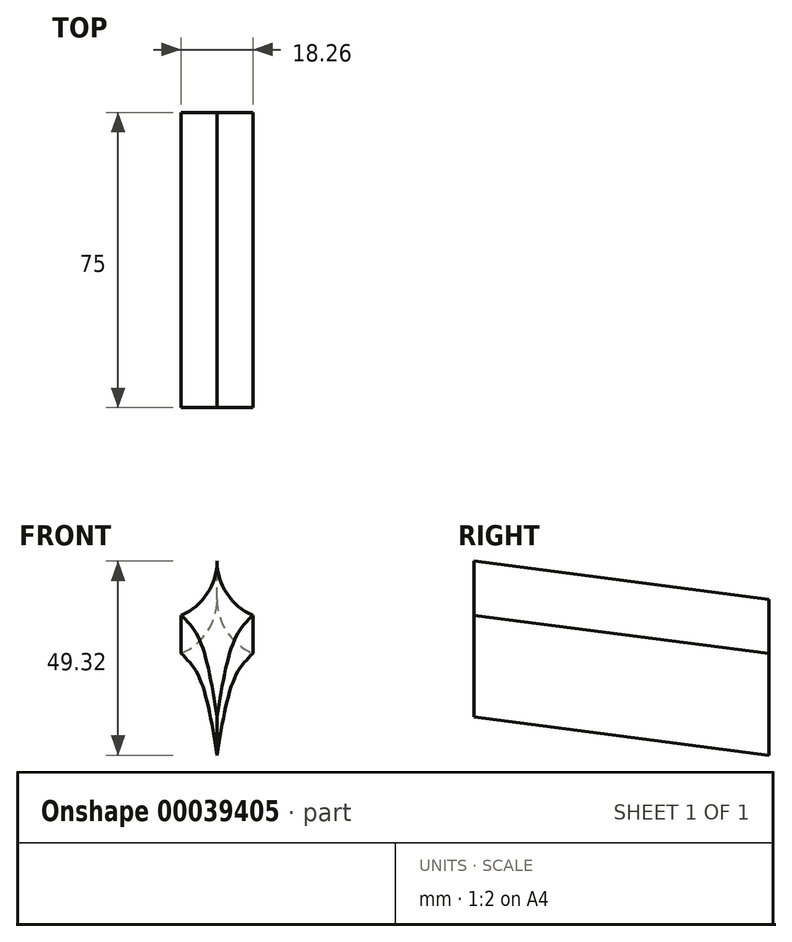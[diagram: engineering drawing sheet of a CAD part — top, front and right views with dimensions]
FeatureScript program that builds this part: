
annotation { "Feature Type Name" : "Feature", "Feature Type Description" : "" }
export const myFeature = defineFeature(function(context is Context, id is Id, definition is map)
    precondition{}
    {
        {
            var Q0;
            Q0=qCreatedBy(makeId("Front.planeOp"),FACE);
            cPlane(context, id + "F0", {"entities" : qUnion([Q0]), "cplaneType" : CPlaneType.OFFSET, "offset" : 75 * mm, "width" : 150 * mm, "height" : 150 * mm});
        }
        {
            var Q0;
            Q0=qCreatedBy(makeId("Front.planeOp"),FACE);
            var sketch = newSketch(context, id + "F1", { "sketchPlane" : qUnion([Q0])});
            skArc(sketch, "E0", {"start": v(-30.39, 0) * mm, "mid": v(-15.2, -15.02) * mm, "end": v(0, 0) * mm});
            skLineSegment(sketch, "E1", {"start": v(-30.39, 0) * mm, "end": v(0, 0) * mm});
            skLineSegment(sketch, "E2", {"start": v(0, 0) * mm, "end": v(0, 0) * mm});
            skLineSegment(sketch, "E3.MirrorCS", {"start": v(30.39, 0) * mm, "end": v(0, 0) * mm});
            skArc(sketch, "E4.MirrorCS", {"start": v(30.39, 0) * mm, "mid": v(15.2, -15.02) * mm, "end": v(0, 0) * mm});
            skFitSpline(sketch, "E5", {"points": [v(-9.13, -13.76) * mm, v(-4.57, -19.76) * mm, v(0, -39.62) * mm], "startDerivative": vector(12.95, -12.86) * mm, "endDerivative": vector(5.88, -36.94) * mm});
            skFitSpline(sketch, "E6.MirrorCS", {"points": [v(9.13, -13.76) * mm, v(4.57, -19.76) * mm, v(0, -39.62) * mm], "startDerivative": vector(-12.95, -12.86) * mm, "endDerivative": vector(-5.88, -36.94) * mm});
            skLineSegment(sketch, "E7", {"start": v(0, 0) * mm, "end": v(0, -39.62) * mm});
            skArc(sketch, "E8", {"start": v(0, 0) * mm, "mid": v(2.49, -8.25) * mm, "end": v(9.13, -13.76) * mm});
            skArc(sketch, "E9", {"start": v(-9.13, -13.76) * mm, "mid": v(-2.49, -8.25) * mm, "end": v(0, 0) * mm});
            skSolve(sketch);
        }
        {
            var Q0;
            Q0=qCreatedBy(id+"F0.planeOp",FACE);
            var sketch = newSketch(context, id + "F2", { "sketchPlane" : qUnion([Q0])});
            skArc(sketch, "E10", {"start": v(-30.39, 9.7) * mm, "mid": v(-15.2, -5.32) * mm, "end": v(0, 9.7) * mm});
            skLineSegment(sketch, "E11", {"start": v(-30.39, 9.7) * mm, "end": v(0, 9.7) * mm});
            skLineSegment(sketch, "E12", {"start": v(0, 9.7) * mm, "end": v(0, 9.7) * mm});
            skLineSegment(sketch, "E13.MirrorCS", {"start": v(30.39, 9.7) * mm, "end": v(0, 9.7) * mm});
            skArc(sketch, "E14.MirrorCS", {"start": v(30.39, 9.7) * mm, "mid": v(15.2, -5.32) * mm, "end": v(0, 9.7) * mm});
            skFitSpline(sketch, "E15", {"points": [v(-9.13, -4.06) * mm, v(-4.57, -10.06) * mm, v(0, -29.92) * mm], "startDerivative": vector(12.95, -12.86) * mm, "endDerivative": vector(5.88, -36.94) * mm});
            skFitSpline(sketch, "E16.MirrorCS", {"points": [v(9.13, -4.06) * mm, v(4.57, -10.06) * mm, v(0, -29.92) * mm], "startDerivative": vector(-12.95, -12.86) * mm, "endDerivative": vector(-5.88, -36.94) * mm});
            skLineSegment(sketch, "E17", {"start": v(0, 9.7) * mm, "end": v(0, -29.92) * mm});
            skArc(sketch, "E18", {"start": v(0, 9.7) * mm, "mid": v(2.49, 1.44) * mm, "end": v(9.13, -4.06) * mm});
            skArc(sketch, "E19", {"start": v(-9.13, -4.06) * mm, "mid": v(-2.49, 1.44) * mm, "end": v(0, 9.7) * mm});
            skSolve(sketch);
        }
        {
            var Q0;
            Q0=sQuery(id+"F1.wireOp",EDGE,"E1");
            var Q1;
            Q1=sQuery(id+"F2.wireOp",EDGE,"E11");
            loft(context, id + "F3", {"bodyType" : ToolBodyType.SURFACE, "wireProfilesArray" : [{ "wireProfileEntities" : qUnion([Q0]) }, { "wireProfileEntities" : qUnion([Q1]) }]});
        }
        {
            var Q0;
            {var subQ3=sQuery(id+"F1.wireOp",EDGE,"E1");Q0=makeQuery(id+"F1.imprint","IMPRINT",FACE,{"disambiguationData":[TD([[makeQuery(id+"F1.imprint","IMPRINT",EDGE,{"derivedFrom":subQ3}),-1.0]])]});}
            var Q1;
            {var subQ0=sQuery(id+"F2.wireOp",EDGE,"E11");Q1=makeQuery(id+"F2.imprint","IMPRINT",FACE,{"disambiguationData":[TD([[makeQuery(id+"F2.imprint","IMPRINT",EDGE,{"derivedFrom":subQ0}),-1.0]])]});}
            var Q2;
            Q2=sQuery(id+"F1.wireOp",EDGE,"E0");
            var Q3;
            Q3=sQuery(id+"F2.wireOp",EDGE,"E10");
            loft(context, id + "F4", {"bodyType" : ToolBodyType.SURFACE, "sheetProfilesArray" : [{ "sheetProfileEntities" : qUnion([Q0]) }, { "sheetProfileEntities" : qUnion([Q1]) }], "wireProfilesArray" : [{ "wireProfileEntities" : qUnion([Q2]) }, { "wireProfileEntities" : qUnion([Q3]) }]});
        }
        {
            var Q0;
            Q0=sQuery(id+"F1.wireOp",EDGE,"E3.MirrorCS");
            var Q1;
            Q1=sQuery(id+"F2.wireOp",EDGE,"E13.MirrorCS");
            loft(context, id + "F5", {"bodyType" : ToolBodyType.SURFACE, "wireProfilesArray" : [{ "wireProfileEntities" : qUnion([Q0]) }, { "wireProfileEntities" : qUnion([Q1]) }]});
        }
        {
            var Q0;
            Q0=sQuery(id+"F1.wireOp",EDGE,"E4.MirrorCS");
            var Q1;
            Q1=sQuery(id+"F2.wireOp",EDGE,"E14.MirrorCS");
            loft(context, id + "F6", {"bodyType" : ToolBodyType.SURFACE, "wireProfilesArray" : [{ "wireProfileEntities" : qUnion([Q0]) }, { "wireProfileEntities" : qUnion([Q1]) }]});
        }
        {
            var Q0;
            Q0=makeQuery(id+"F3.opLoft","MID_CAP_EDGE",EDGE,{"disambiguationData":[OSD([sQuery(id+"F1.wireOp",VERTEX,"E1.start"),sQuery(id+"F1.wireOp",VERTEX,"E1.end"),sQuery(id+"F1.wireOp",EDGE,"E1")])],"capPos":0.0});
            var Q1;
            Q1=makeQuery(id+"F4.opLoft","MID_CAP_EDGE",EDGE,{"disambiguationData":[OSD([sQuery(id+"F1.wireOp",VERTEX,"E0.start"),sQuery(id+"F1.wireOp",VERTEX,"E0.end"),sQuery(id+"F1.wireOp",EDGE,"E0")])],"capPos":0.0});
            loft(context, id + "F7", {"bodyType" : ToolBodyType.SURFACE, "wireProfilesArray" : [{ "wireProfileEntities" : qUnion([Q0]) }, { "wireProfileEntities" : qUnion([Q1]) }]});
        }
        {
            var Q0;
            Q0=makeQuery(id+"F3.opLoft","MID_CAP_EDGE",EDGE,{"disambiguationData":[OSD([sQuery(id+"F2.wireOp",VERTEX,"E11.start"),sQuery(id+"F2.wireOp",VERTEX,"E11.end"),sQuery(id+"F2.wireOp",EDGE,"E11")])],"capPos":1.0});
            var Q1;
            Q1=makeQuery(id+"F4.opLoft","MID_CAP_EDGE",EDGE,{"disambiguationData":[OSD([sQuery(id+"F2.wireOp",VERTEX,"E10.start"),sQuery(id+"F2.wireOp",VERTEX,"E10.end"),sQuery(id+"F2.wireOp",EDGE,"E10")])],"capPos":1.0});
            loft(context, id + "F8", {"bodyType" : ToolBodyType.SURFACE, "wireProfilesArray" : [{ "wireProfileEntities" : qUnion([Q0]) }, { "wireProfileEntities" : qUnion([Q1]) }]});
        }
        {
            var Q0;
            Q0=makeQuery(id+"F5.opLoft","MID_CAP_EDGE",EDGE,{"disambiguationData":[OSD([sQuery(id+"F2.wireOp",VERTEX,"E13.MirrorCS.start"),sQuery(id+"F2.wireOp",VERTEX,"E13.MirrorCS.end"),sQuery(id+"F2.wireOp",EDGE,"E13.MirrorCS")])],"capPos":1.0});
            var Q1;
            Q1=makeQuery(id+"F6.opLoft","MID_CAP_EDGE",EDGE,{"disambiguationData":[OSD([sQuery(id+"F2.wireOp",VERTEX,"E14.MirrorCS.start"),sQuery(id+"F2.wireOp",VERTEX,"E14.MirrorCS.end"),sQuery(id+"F2.wireOp",EDGE,"E14.MirrorCS")])],"capPos":1.0});
            loft(context, id + "F9", {"bodyType" : ToolBodyType.SURFACE, "wireProfilesArray" : [{ "wireProfileEntities" : qUnion([Q0]) }, { "wireProfileEntities" : qUnion([Q1]) }]});
        }
        {
            var Q0;
            Q0=makeQuery(id+"F5.opLoft","MID_CAP_EDGE",EDGE,{"disambiguationData":[OSD([sQuery(id+"F1.wireOp",VERTEX,"E3.MirrorCS.start"),sQuery(id+"F1.wireOp",VERTEX,"E3.MirrorCS.end"),sQuery(id+"F1.wireOp",EDGE,"E3.MirrorCS")])],"capPos":0.0});
            var Q1;
            Q1=makeQuery(id+"F6.opLoft","MID_CAP_EDGE",EDGE,{"disambiguationData":[OSD([sQuery(id+"F1.wireOp",VERTEX,"E4.MirrorCS.start"),sQuery(id+"F1.wireOp",VERTEX,"E4.MirrorCS.end"),sQuery(id+"F1.wireOp",EDGE,"E4.MirrorCS")])],"capPos":0.0});
            loft(context, id + "F10", {"bodyType" : ToolBodyType.SURFACE, "wireProfilesArray" : [{ "wireProfileEntities" : qUnion([Q0]) }, { "wireProfileEntities" : qUnion([Q1]) }]});
        }
        {
            var Q0;
            Q0=makeQuery(id+"F1.imprint","IMPRINT",FACE,{"disambiguationData":[TD([[makeQuery(id+"F1.imprint","IMPRINT",EDGE,{"derivedFrom":sQuery(id+"F1.wireOp",EDGE,"E5")}),1.0]])]});
            var Q1;
            Q1=makeQuery(id+"F2.imprint","IMPRINT",FACE,{"disambiguationData":[TD([[makeQuery(id+"F2.imprint","IMPRINT",EDGE,{"derivedFrom":sQuery(id+"F2.wireOp",EDGE,"E15")}),1.0]])]});
            loft(context, id + "F11", {"sheetProfilesArray" : [{ "sheetProfileEntities" : qUnion([Q0]) }, { "sheetProfileEntities" : qUnion([Q1]) }]});
        }
        {
            var Q1;
            Q1=makeQuery(id+"F1.imprint","IMPRINT",FACE,{"disambiguationData":[TD([[makeQuery(id+"F1.imprint","IMPRINT",EDGE,{"derivedFrom":sQuery(id+"F1.wireOp",EDGE,"E6.MirrorCS")}),-1.0]])]});
            var Q2;
            Q2=makeQuery(id+"F2.imprint","IMPRINT",FACE,{"disambiguationData":[TD([[makeQuery(id+"F2.imprint","IMPRINT",EDGE,{"derivedFrom":sQuery(id+"F2.wireOp",EDGE,"E16.MirrorCS")}),-1.0]])]});
            loft(context, id + "F12", {"operationType" : NewBodyOperationType.ADD, "sheetProfilesArray" : [{ "sheetProfileEntities" : qUnion([Q1]) }, { "sheetProfileEntities" : qUnion([Q2]) }]});
        }
    });
